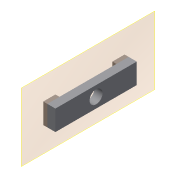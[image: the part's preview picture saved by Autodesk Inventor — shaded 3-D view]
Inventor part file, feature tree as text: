
AUTODESK INVENTOR PART (.ipt)
format: ipt  version: 2019 (Build 230136000, 136)  size: 102,912 bytes
history: native  units: mm
features: other x3, extrude x2, sketch x2, plane x1, reference x1, projected_geometry x1
ambient origin geometry x8: Origin, YZ Plane, XZ Plane, XY Plane, X Axis, Y Axis, Z Axis, Center Point
bodies: Volumenkörper1 (feature_tree)
feature tree (10):
  plane  "Arbeitsebene1"
  extrude  "Extrusion1"  Depth=20.0mm
  extrude  "Extrusion2"  Depth=1.0mm
  sketch  "Skizze1"  dims[d0=5.0mm d1=20.0mm]
  reference  "Referenz1"
  sketch  "Skizze2"  dims[d2=2.0mm d3=0.0mm d4=0.2mm d5=3.0mm d6=3.0mm d7=1.0mm d8=0.0mm]
  projected_geometry  "Projizierte Kontur1"
  other  "<userpath>\Documents\Inventor\HITscope\Assembly_Omniscope_v1.iam"
  other  "Assembly_Omniscope_v1.iam"
  other  "01_Camera_Module_left_v0:1"
